annotation { "Feature Type Name" : "Feature", "Feature Type Description" : "" }
export const myFeature = defineFeature(function(context is Context, id is Id, definition is map)
    precondition{}
    {
        {
            var Q0;
            Q0=qCreatedBy(makeId("Top.planeOp"),FACE);
            var sketch = newSketch(context, id + "F0", { "sketchPlane" : qUnion([Q0])});
            skLineSegment(sketch, "E0.bottom", {"start": v(-24.08, 16.12) * mm, "end": v(15.92, 16.12) * mm});
            skLineSegment(sketch, "E0.top", {"start": v(-24.08, -23.88) * mm, "end": v(15.92, -23.88) * mm});
            skLineSegment(sketch, "E0.left", {"start": v(-24.08, 16.12) * mm, "end": v(-24.08, -23.88) * mm});
            skLineSegment(sketch, "E0.right", {"start": v(15.92, 16.12) * mm, "end": v(15.92, -23.88) * mm});
            skSolve(sketch);
        }
        {
            var Q0;
            Q0 = qSketchRegion(id + "F0", true);
            extrude(context, id + "F1", {"entities" : qUnion([Q0]), "endBound" : BoundingType.SYMMETRIC, "depth" : 40 * mm, "offsetDistance" : 25.4 * mm});
        }
        {
            var Q0;
            Q0=makeQuery(id+"F1.opExtrude","SWEPT_FACE",FACE,{"disambiguationData":[OSD([sQuery(id+"F0.wireOp",EDGE,"E0.top")])]});
            var sketch = newSketch(context, id + "F2", { "sketchPlane" : qUnion([Q0])});
            skArc(sketch, "E1", {"start": v(15.92, 13.2) * mm, "mid": v(8.94, 17.41) * mm, "end": v(1.2, 20) * mm});
            skArc(sketch, "E2", {"start": v(-9.64, 20) * mm, "mid": v(-16.26, 17.13) * mm, "end": v(-21.6, 12.28) * mm});
            skLineSegment(sketch, "E3", {"start": v(-9.64, 20) * mm, "end": v(1.2, 20) * mm});
            skLineSegment(sketch, "E4", {"start": v(15.92, 7.56) * mm, "end": v(15.92, 13.2) * mm});
            skFitSpline(sketch, "E5", {"points": [v(-16.1, 9.25) * mm, v(-12.24, 13.33) * mm, v(1.2, 13.75) * mm, v(15.92, 7.56) * mm], "startDerivative": vector(12.04, 19.82) * mm, "endDerivative": vector(35.27, -18.86) * mm});
            skFitSpline(sketch, "E6", {"points": [v(-16.1, 9.25) * mm, v(-5.13, 3.9) * mm, v(11.82, 1.1) * mm, v(15.92, -3.27) * mm, v(15.92, -8.48) * mm, v(14.14, -16) * mm, v(4.08, -20) * mm, v(4.5, -20) * mm], "startDerivative": vector(52.31, -34.93) * mm, "endDerivative": vector(20.25, 1.34) * mm});
            skArc(sketch, "E7", {"start": v(-24.08, -12.07) * mm, "mid": v(-18.65, -17.56) * mm, "end": v(-11.32, -20) * mm});
            skLineSegment(sketch, "E8", {"start": v(-24.08, -12.07) * mm, "end": v(-19.41, -8.62) * mm});
            skFitSpline(sketch, "E9", {"points": [v(-19.41, -8.62) * mm, v(-11.04, -12.63) * mm, v(6.69, -11.78) * mm, v(7.81, -4.6) * mm, v(-4.3, -1.4) * mm, v(-16.39, 0) * mm, v(-21.03, 5.38) * mm], "startDerivative": vector(43.1, -28.67) * mm, "endDerivative": vector(-27.3, 46.94) * mm});
            skFitSpline(sketch, "E10", {"points": [v(-21.03, 5.38) * mm, v(-22.35, 8.55) * mm, v(-21.6, 12.28) * mm], "startDerivative": vector(-3.73, 6.31) * mm, "endDerivative": vector(2.55, 7.47) * mm});
            skLineSegment(sketch, "E11", {"start": v(-19.41, -8.62) * mm, "end": v(-19.41, -17.06) * mm});
            skSolve(sketch);
        }
        {
            var Q0;
            Q0 = qSketchRegion(id + "F2", true);
            var Q1;
            {var subQ4=sQuery(id+"F2.wireOp",EDGE,"E2");Q1=makeQuery(id+"F2.imprint","IMPRINT",FACE,{"disambiguationData":[TD([[makeQuery(id+"F2.imprint","IMPRINT",EDGE,{"derivedFrom":subQ4}),-1.0]])]});}
            var Q2;
            {var subQ0=sQuery(id+"F2.wireOp",EDGE,"E5");Q2=makeQuery(id+"F2.imprint","IMPRINT",FACE,{"disambiguationData":[TD([[makeQuery(id+"F2.imprint","IMPRINT",EDGE,{"derivedFrom":subQ0}),-1.0]])]});}
            var Q3;
            {var subQ0=sQuery(id+"F2.wireOp",EDGE,"E1");Q3=makeQuery(id+"F2.imprint","IMPRINT",FACE,{"disambiguationData":[TD([[makeQuery(id+"F2.imprint","IMPRINT",EDGE,{"derivedFrom":subQ0}),-1.0]])]});}
            var Q4;
            {var subQ0=sQuery(id+"F2.wireOp",EDGE,"E7");Q4=makeQuery(id+"F2.imprint","IMPRINT",FACE,{"disambiguationData":[TD([[makeQuery(id+"F2.imprint","IMPRINT",EDGE,{"derivedFrom":subQ0}),-1.0]])]});}
            var Q5;
            {var subQ0=sQuery(id+"F2.wireOp",EDGE,"E6");var subQ1=sQuery(id+"F0.wireOp",EDGE,"E0.top");var subQ4=makeQuery(id+"F1.opExtrude","CAP_EDGE",EDGE,{"disambiguationData":[OSD([subQ1])],"isStart":true});var subQ7=makeQuery(id+"F2.imprint","INTERSECT",VERTEX,{"disambiguationData":[OD(0.0)],"derivedFrom":[subQ4,subQ0]});Q5=makeQuery(id+"F2.imprint","IMPRINT",FACE,{"disambiguationData":[TD([[makeQuery(id+"F2.imprint","IMPRINT",EDGE,{"disambiguationData":[TD([[subQ7,1.0]])],"derivedFrom":subQ4}),1.0]])]});}
            extrude(context, id + "F3", {"entities" : qUnion([Q0, Q1, Q2, Q3, Q4, Q5]), "operationType" : NewBodyOperationType.REMOVE, "oppositeDirection" : true, "depth" : 40 * mm, "offsetDistance" : 25.4 * mm});
        }
        {
            var Q0;
            Q0=makeQuery(id+"F1.opExtrude","CAP_FACE",FACE,{"disambiguationData":[OSD([sQuery(id+"F0.wireOp",EDGE,"E0.bottom"),sQuery(id+"F0.wireOp",EDGE,"E0.top"),sQuery(id+"F0.wireOp",EDGE,"E0.left"),sQuery(id+"F0.wireOp",EDGE,"E0.right")])],"isStart":false});
            var sketch = newSketch(context, id + "F4", { "sketchPlane" : qUnion([Q0])});
            skLineSegment(sketch, "E12.bottom", {"start": v(-24.48, 15.64) * mm, "end": v(16.46, 15.64) * mm});
            skLineSegment(sketch, "E12.top", {"start": v(-24.48, -24.32) * mm, "end": v(16.46, -24.32) * mm});
            skLineSegment(sketch, "E12.left", {"start": v(-24.48, 15.64) * mm, "end": v(-24.48, -24.32) * mm});
            skLineSegment(sketch, "E12.right", {"start": v(16.46, 15.64) * mm, "end": v(16.46, -24.32) * mm});
            skLineSegment(sketch, "E13", {"start": v(-24.48, 8.4) * mm, "end": v(-9.64, -3.14) * mm});
            skLineSegment(sketch, "E14", {"start": v(-9.64, -3.14) * mm, "end": v(-24.48, -24.32) * mm});
            skLineSegment(sketch, "E15", {"start": v(16.46, 8.4) * mm, "end": v(-3.3, -24.32) * mm});
            skLineSegment(sketch, "E16", {"start": v(-16.42, 15.64) * mm, "end": v(-2.08, 4.5) * mm});
            skLineSegment(sketch, "E17", {"start": v(-2.08, 4.5) * mm, "end": v(5.74, 15.64) * mm});
            skArc(sketch, "E18", {"start": v(-10.48, -24.32) * mm, "mid": v(-5.96, -23.72) * mm, "end": v(-1.8, -21.85) * mm});
            skSolve(sketch);
        }
        {
            var Q0;
            {var subQ2=sQuery(id+"F4.wireOp",EDGE,"E13");Q0=makeQuery(id+"F4.imprint","IMPRINT",FACE,{"disambiguationData":[TD([[makeQuery(id+"F4.imprint","IMPRINT",EDGE,{"derivedFrom":subQ2}),-1.0]])]});}
            var Q1;
            {var subQ5=sQuery(id+"F4.wireOp",EDGE,"E16");var subQ7=sQuery(id+"F4.wireOp",EDGE,"E17");var subQ8=makeQuery(id+"F4.imprint","INTERSECT",VERTEX,{"derivedFrom":[subQ5,subQ7]});Q1=makeQuery(id+"F4.imprint","IMPRINT",FACE,{"disambiguationData":[TD([[makeQuery(id+"F4.imprint","IMPRINT",EDGE,{"disambiguationData":[TD([[subQ8,1.0]])],"derivedFrom":subQ5}),1.0]])]});}
            var Q2;
            {var subQ1=sQuery(id+"F4.wireOp",EDGE,"E12.right");var subQ6=sQuery(id+"F4.wireOp",EDGE,"E12.top");var subQ10=makeQuery(id+"F4.imprint","INTERSECT",VERTEX,{"derivedFrom":[subQ6,subQ1]});Q2=makeQuery(id+"F4.imprint","IMPRINT",FACE,{"disambiguationData":[TD([[makeQuery(id+"F4.imprint","IMPRINT",EDGE,{"disambiguationData":[TD([[subQ10,1.0]])],"derivedFrom":subQ6}),1.0]])]});}
            var Q3;
            {var subQ0=sQuery(id+"F4.wireOp",EDGE,"E15");var subQ1=sQuery(id+"F0.wireOp",EDGE,"E0.top");var subQ4=makeQuery(id+"F1.opExtrude","CAP_EDGE",EDGE,{"disambiguationData":[OSD([subQ1])],"isStart":false});var subQ5=makeQuery(id+"F4.imprint","INTERSECT",VERTEX,{"derivedFrom":[subQ4,subQ0]});Q3=makeQuery(id+"F4.imprint","IMPRINT",FACE,{"disambiguationData":[TD([[makeQuery(id+"F4.imprint","IMPRINT",EDGE,{"disambiguationData":[TD([[subQ5,1.0]])],"derivedFrom":subQ0}),1.0]])]});}
            var Q4;
            {var subQ0=sQuery(id+"F4.wireOp",EDGE,"E18");var subQ1=sQuery(id+"F4.wireOp",EDGE,"E15");var subQ2=makeQuery(id+"F4.imprint","INTERSECT",VERTEX,{"derivedFrom":[subQ1,subQ0]});Q4=makeQuery(id+"F4.imprint","IMPRINT",FACE,{"disambiguationData":[TD([[makeQuery(id+"F4.imprint","IMPRINT",EDGE,{"disambiguationData":[TD([[subQ2,-1.0]])],"derivedFrom":subQ1}),-1.0]])]});}
            extrude(context, id + "F5", {"entities" : qUnion([Q0, Q1, Q2, Q3, Q4]), "operationType" : NewBodyOperationType.REMOVE, "oppositeDirection" : true, "depth" : 40 * mm, "offsetDistance" : 25.4 * mm});
        }
        {
            var Q0;
            Q0=makeQuery(id+"F5.boolean.opBoolean","SPLIT",FACE,{"disambiguationData":[TD([makeQuery(id+"F1.opExtrude","SWEPT_FACE",FACE,{"disambiguationData":[OSD([sQuery(id+"F0.wireOp",EDGE,"E0.bottom")])]})])],"derivedFrom":makeQuery(id+"F3.boolean.opBoolean","COPY",FACE,{"derivedFrom":makeQuery(id+"F3.opExtrude","SWEPT_FACE",FACE,{"disambiguationData":[OSD([sQuery(id+"F2.wireOp",EDGE,"E11")])]})})});
            var sketch = newSketch(context, id + "F6", { "sketchPlane" : qUnion([Q0])});
            skLineSegment(sketch, "E19.bottom", {"start": v(-17, 20.65) * mm, "end": v(25.07, 20.65) * mm});
            skLineSegment(sketch, "E19.top", {"start": v(-17, -20.23) * mm, "end": v(25.07, -20.23) * mm});
            skLineSegment(sketch, "E19.left", {"start": v(-17, 20.65) * mm, "end": v(-17, -20.23) * mm});
            skLineSegment(sketch, "E19.right", {"start": v(25.07, 20.65) * mm, "end": v(25.07, -20.23) * mm});
            skLineSegment(sketch, "E20.bottom", {"start": v(-16.1, 20.02) * mm, "end": v(-1.8, 20.02) * mm});
            skLineSegment(sketch, "E20.top", {"start": v(-16.1, -20.23) * mm, "end": v(-1.8, -20.23) * mm});
            skLineSegment(sketch, "E20.left", {"start": v(-16.1, 20.02) * mm, "end": v(-16.1, -20.23) * mm});
            skLineSegment(sketch, "E20.right", {"start": v(-1.8, 20.02) * mm, "end": v(-1.8, -20.23) * mm});
            skLineSegment(sketch, "E21", {"start": v(-1.8, 2.69) * mm, "end": v(25.07, 15.16) * mm});
            skLineSegment(sketch, "E22", {"start": v(25.07, 15.16) * mm, "end": v(25.07, 4.9) * mm});
            skLineSegment(sketch, "E23", {"start": v(25.07, 4.9) * mm, "end": v(-1.8, -5.37) * mm});
            skLineSegment(sketch, "E24", {"start": v(2.3, -20.23) * mm, "end": v(10.98, -20.23) * mm});
            skLineSegment(sketch, "E25", {"start": v(2.07, -3.89) * mm, "end": v(8.31, -20.23) * mm});
            skLineSegment(sketch, "E26", {"start": v(-1.8, -5.37) * mm, "end": v(-6.32, -7.16) * mm});
            skLineSegment(sketch, "E27", {"start": v(1.37, -20.23) * mm, "end": v(-4.06, -6.53) * mm});
            skPoint(sketch, "E27.endSnap0", {"position": v(-4.06, -6.26) * mm});
            skLineSegment(sketch, "E28", {"start": v(-4.06, -6.53) * mm, "end": v(-4.06, -6.26) * mm});
            skSolve(sketch);
        }
        {
            var Q0;
            {var subQ11=sQuery(id+"F6.wireOp",EDGE,"E19.bottom");Q0=makeQuery(id+"F6.imprint","IMPRINT",FACE,{"disambiguationData":[TD([[makeQuery(id+"F6.imprint","IMPRINT",EDGE,{"derivedFrom":subQ11}),-1.0]])]});}
            var Q1;
            {var subQ3=sQuery(id+"F6.wireOp",EDGE,"E25");Q1=makeQuery(id+"F6.imprint","IMPRINT",FACE,{"disambiguationData":[TD([[makeQuery(id+"F6.imprint","IMPRINT",EDGE,{"derivedFrom":subQ3}),1.0]])]});}
            var Q2;
            {var subQ1=sQuery(id+"F6.wireOp",EDGE,"E19.top");var subQ3=sQuery(id+"F6.wireOp",EDGE,"E27");var subQ4=makeQuery(id+"F6.imprint","INTERSECT",VERTEX,{"derivedFrom":[subQ1,subQ3]});Q2=makeQuery(id+"F6.imprint","IMPRINT",FACE,{"disambiguationData":[TD([[makeQuery(id+"F6.imprint","IMPRINT",EDGE,{"disambiguationData":[TD([[subQ4,-1.0]])],"derivedFrom":subQ3}),1.0]])]});}
            extrude(context, id + "F7", {"entities" : qUnion([Q0, Q1, Q2]), "operationType" : NewBodyOperationType.REMOVE, "oppositeDirection" : true, "depth" : 40 * mm, "offsetDistance" : 25.4 * mm});
        }
        {
            var Q0;
            {var subQ2=sQuery(id+"F0.wireOp",EDGE,"E0.top");Q0=makeQuery(id+"F5.boolean.opBoolean","SPLIT",FACE,{"disambiguationData":[TD([makeQuery(id+"F1.opExtrude","SWEPT_FACE",FACE,{"disambiguationData":[OSD([subQ2])]})])],"derivedFrom":makeQuery(id+"F1.opExtrude","CAP_FACE",FACE,{"disambiguationData":[OSD([sQuery(id+"F0.wireOp",EDGE,"E0.bottom"),subQ2,sQuery(id+"F0.wireOp",EDGE,"E0.left"),sQuery(id+"F0.wireOp",EDGE,"E0.right")])],"isStart":false})});}
            var sketch = newSketch(context, id + "F8", { "sketchPlane" : qUnion([Q0])});
            skLineSegment(sketch, "E29.bottom", {"start": v(-26.5, -12.4) * mm, "end": v(-1.14, -12.4) * mm});
            skLineSegment(sketch, "E29.top", {"start": v(-26.5, -25.13) * mm, "end": v(-1.14, -25.13) * mm});
            skLineSegment(sketch, "E29.left", {"start": v(-26.5, -12.4) * mm, "end": v(-26.5, -25.13) * mm});
            skLineSegment(sketch, "E29.right", {"start": v(-1.14, -12.4) * mm, "end": v(-1.14, -25.13) * mm});
            skLineSegment(sketch, "E30.bottom", {"start": v(-9.63, 17.34) * mm, "end": v(1.16, 17.34) * mm});
            skLineSegment(sketch, "E30.top", {"start": v(-9.63, 14.08) * mm, "end": v(1.16, 14.08) * mm});
            skLineSegment(sketch, "E30.left", {"start": v(-9.63, 17.34) * mm, "end": v(-9.63, 14.08) * mm});
            skLineSegment(sketch, "E30.right", {"start": v(1.16, 17.34) * mm, "end": v(1.16, 14.08) * mm});
            skSolve(sketch);
        }
        {
            var Q0;
            Q0 = qSketchRegion(id + "F8", true);
            extrude(context, id + "F9", {"entities" : qUnion([Q0]), "operationType" : NewBodyOperationType.REMOVE, "oppositeDirection" : true, "depth" : 10 * mm, "offsetDistance" : 25.4 * mm});
        }
        {
            var Q0;
            {var subQ2=sQuery(id+"F0.wireOp",EDGE,"E0.top");Q0=makeQuery(id+"F5.boolean.opBoolean","SPLIT",FACE,{"disambiguationData":[TD([makeQuery(id+"F1.opExtrude","SWEPT_FACE",FACE,{"disambiguationData":[OSD([subQ2])]})])],"derivedFrom":makeQuery(id+"F1.opExtrude","CAP_FACE",FACE,{"disambiguationData":[OSD([sQuery(id+"F0.wireOp",EDGE,"E0.bottom"),subQ2,sQuery(id+"F0.wireOp",EDGE,"E0.left"),sQuery(id+"F0.wireOp",EDGE,"E0.right")])],"isStart":false})});}
            var sketch = newSketch(context, id + "F10", { "sketchPlane" : qUnion([Q0])});
            skLineSegment(sketch, "E31.bottom", {"start": v(-9.64, 16.24) * mm, "end": v(1.18, 16.24) * mm});
            skLineSegment(sketch, "E31.top", {"start": v(-9.64, 15.46) * mm, "end": v(1.18, 15.46) * mm});
            skLineSegment(sketch, "E31.left", {"start": v(-9.64, 16.24) * mm, "end": v(-9.64, 15.46) * mm});
            skLineSegment(sketch, "E31.right", {"start": v(1.18, 16.24) * mm, "end": v(1.18, 15.46) * mm});
            skSolve(sketch);
        }
        {
            var Q0;
            Q0 = qSketchRegion(id + "F10", true);
            extrude(context, id + "F11", {"entities" : qUnion([Q0]), "operationType" : NewBodyOperationType.REMOVE, "oppositeDirection" : true, "depth" : 40 * mm, "offsetDistance" : 25.4 * mm});
        }
        {
            var Q0;
            Q0=makeQuery(id+"F9.boolean.opBoolean","COPY",FACE,{"derivedFrom":makeQuery(id+"F9.opExtrude","CAP_FACE",FACE,{"disambiguationData":[OSD([sQuery(id+"F8.wireOp",EDGE,"E29.bottom"),sQuery(id+"F8.wireOp",EDGE,"E29.top"),sQuery(id+"F8.wireOp",EDGE,"E29.left"),sQuery(id+"F8.wireOp",EDGE,"E29.right")])],"isStart":false})});
            var sketch = newSketch(context, id + "F12", { "sketchPlane" : qUnion([Q0])});
            skLineSegment(sketch, "E32.bottom", {"start": v(-23.84, -19.9) * mm, "end": v(0, -19.9) * mm});
            skLineSegment(sketch, "E32.top", {"start": v(-23.84, -24.7) * mm, "end": v(0, -24.7) * mm});
            skLineSegment(sketch, "E32.left", {"start": v(-23.84, -19.9) * mm, "end": v(-23.84, -24.7) * mm});
            skLineSegment(sketch, "E32.right", {"start": v(0, -19.9) * mm, "end": v(0, -24.7) * mm});
            skSolve(sketch);
        }
        {
            var Q0;
            Q0 = qSketchRegion(id + "F12", true);
            extrude(context, id + "F13", {"entities" : qUnion([Q0]), "operationType" : NewBodyOperationType.REMOVE, "oppositeDirection" : true, "depth" : 40 * mm, "offsetDistance" : 25.4 * mm});
        }
        {
            var Q0;
            Q0=makeQuery(id+"F5.boolean.opBoolean","SPLIT",FACE,{"disambiguationData":[TD([makeQuery(id+"F1.opExtrude","SWEPT_FACE",FACE,{"disambiguationData":[OSD([sQuery(id+"F0.wireOp",EDGE,"E0.bottom")])]})])],"derivedFrom":makeQuery(id+"F3.boolean.opBoolean","COPY",FACE,{"derivedFrom":makeQuery(id+"F3.opExtrude","SWEPT_FACE",FACE,{"disambiguationData":[OSD([sQuery(id+"F2.wireOp",EDGE,"E11")])]})})});
            var sketch = newSketch(context, id + "F14", { "sketchPlane" : qUnion([Q0])});
            skText(sketch, "E33", { "text": "Kiana Yee", "fontName": "OpenSans-Regular.ttf"});
            const initialGuessF14  = {"E33": [-0.01612, -0.01706, 1, 0, 0.00182]};
            skSetInitialGuess(sketch, initialGuessF14);
            skSolve(sketch);
        }
        {
            var Q0;
            Q0 = qSketchRegion(id + "F14", true);
            extrude(context, id + "F15", {"entities" : qUnion([Q0]), "operationType" : NewBodyOperationType.REMOVE, "oppositeDirection" : true, "depth" : 0.5 * mm, "offsetDistance" : 25.4 * mm});
        }
        {
            var Q0;
            {var subQ0=sQuery(id+"F2.wireOp",EDGE,"E11");var subQ2=sQuery(id+"F0.wireOp",EDGE,"E0.bottom");var subQ3=makeQuery(id+"F1.opExtrude","SWEPT_FACE",FACE,{"disambiguationData":[OSD([subQ2])]});var subQ6=makeQuery(id+"F3.boolean.opBoolean","COPY",FACE,{"derivedFrom":makeQuery(id+"F3.opExtrude","SWEPT_FACE",FACE,{"disambiguationData":[OSD([subQ0])]})});Q0=makeQuery(id+"F15.boolean.opBoolean","SPLIT",FACE,{"disambiguationData":[TD([subQ3])],"derivedFrom":makeQuery(id+"F5.boolean.opBoolean","SPLIT",FACE,{"disambiguationData":[TD([subQ3])],"derivedFrom":subQ6})});}
            var sketch = newSketch(context, id + "F16", { "sketchPlane" : qUnion([Q0])});
            skLineSegment(sketch, "E34.bottom", {"start": v(-0.78, -11.36) * mm, "end": v(9.56, -11.36) * mm});
            skLineSegment(sketch, "E34.top", {"start": v(-0.78, -20.58) * mm, "end": v(9.56, -20.58) * mm});
            skLineSegment(sketch, "E34.left", {"start": v(-0.78, -11.36) * mm, "end": v(-0.78, -20.58) * mm});
            skLineSegment(sketch, "E34.right", {"start": v(9.56, -11.36) * mm, "end": v(9.56, -20.58) * mm});
            skLineSegment(sketch, "E35.bottom", {"start": v(-4.46, -8.62) * mm, "end": v(-4.46, -8.62) * mm});
            skLineSegment(sketch, "E35.top", {"start": v(-4.46, -17.06) * mm, "end": v(-4.46, -17.06) * mm});
            skLineSegment(sketch, "E35.left", {"start": v(-4.46, -8.62) * mm, "end": v(-4.46, -17.06) * mm});
            skLineSegment(sketch, "E35.right", {"start": v(-4.46, -8.62) * mm, "end": v(-4.46, -17.06) * mm});
            skLineSegment(sketch, "E36.bottom", {"start": v(-0.78, -17.06) * mm, "end": v(-4.46, -17.06) * mm});
            skLineSegment(sketch, "E36.top", {"start": v(-0.78, -8.62) * mm, "end": v(-4.46, -8.62) * mm});
            skLineSegment(sketch, "E36.left", {"start": v(-0.78, -17.06) * mm, "end": v(-0.78, -8.62) * mm});
            skLineSegment(sketch, "E36.right", {"start": v(-4.46, -17.06) * mm, "end": v(-4.46, -8.62) * mm});
            skSolve(sketch);
        }
        {
            var Q0;
            Q0 = qSketchRegion(id + "F16", true);
            extrude(context, id + "F17", {"entities" : qUnion([Q0]), "operationType" : NewBodyOperationType.REMOVE, "oppositeDirection" : true, "depth" : 20 * mm, "offsetDistance" : 25.4 * mm});
        }
        {
            var Q0;
            {var subQ0=sQuery(id+"F0.wireOp",EDGE,"E0.right");var subQ1=sQuery(id+"F0.wireOp",EDGE,"E0.top");var subQ2=sQuery(id+"F0.wireOp",EDGE,"E0.bottom");var subQ3=makeQuery(id+"F1.opExtrude","CAP_FACE",FACE,{"disambiguationData":[OSD([subQ2,subQ1,sQuery(id+"F0.wireOp",EDGE,"E0.left"),subQ0])],"isStart":true});var subQ9=sQuery(id+"F6.wireOp",EDGE,"E20.right");Q0=makeQuery(id+"F7.boolean.opBoolean","SPLIT",FACE,{"disambiguationData":[TD([makeQuery(id+"F7.opExtrude","SWEPT_FACE",FACE,{"disambiguationData":[OSD([subQ9]),TDD([makeQuery(id+"F6.imprint","IMPRINT",EDGE,{"disambiguationData":[TD([[makeQuery(id+"F6.imprint","INTERSECT",VERTEX,{"derivedFrom":[subQ9,sQuery(id+"F6.wireOp",EDGE,"E27")]}),-1.0]])],"derivedFrom":subQ9})])]})])],"derivedFrom":subQ3});}
            var sketch = newSketch(context, id + "F18", { "sketchPlane" : qUnion([Q0])});
            skCircle(sketch, "E37", {"center": v(6.95, -11.66) * mm, "radius": 1 * mm});
            skSolve(sketch);
        }
        {
            var Q0;
            Q0 = qSketchRegion(id + "F18", true);
            extrude(context, id + "F19", {"entities" : qUnion([Q0]), "operationType" : NewBodyOperationType.REMOVE, "oppositeDirection" : true, "depth" : 4 * mm, "offsetDistance" : 25.4 * mm});
        }
    });